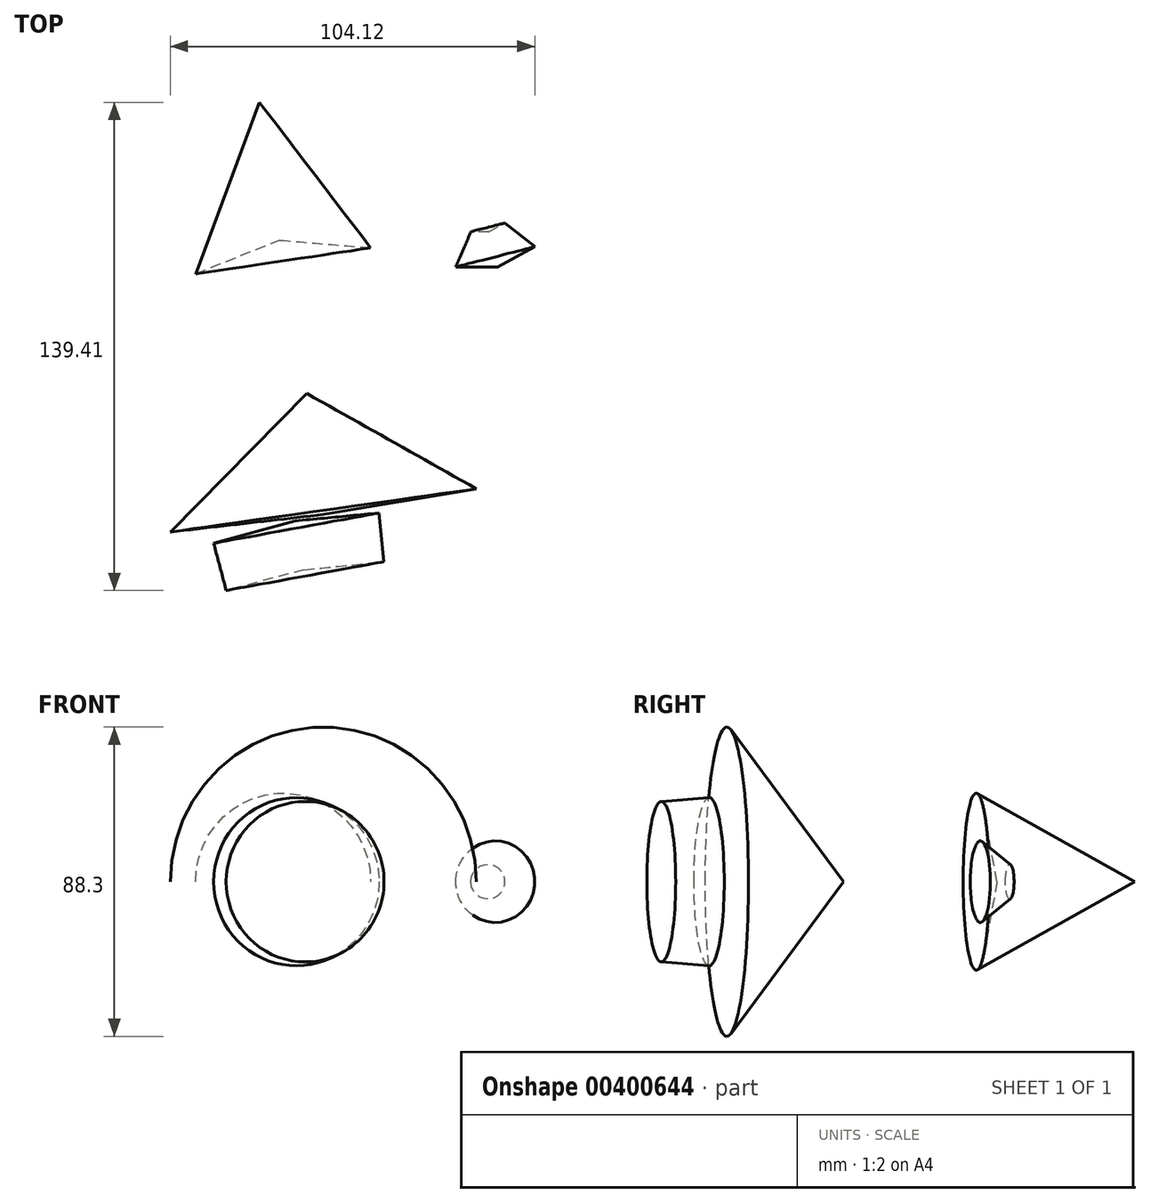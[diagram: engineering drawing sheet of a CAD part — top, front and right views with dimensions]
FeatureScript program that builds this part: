
annotation { "Feature Type Name" : "Feature", "Feature Type Description" : "" }
export const myFeature = defineFeature(function(context is Context, id is Id, definition is map)
    precondition{}
    {
        {
            var Q0;
            Q0=qCreatedBy(makeId("Top.planeOp"),FACE);
            var sketch = newSketch(context, id + "F0", { "sketchPlane" : qUnion([Q0])});
            skLineSegment(sketch, "E0", {"start": v(-35.58, 73.22) * mm, "end": v(-13.14, -77.38) * mm});
            skLineSegment(sketch, "E1", {"start": v(-35.58, 73.22) * mm, "end": v(-3.81, 31.64) * mm});
            skLineSegment(sketch, "E2", {"start": v(-3.81, 31.64) * mm, "end": v(-29.71, 33.85) * mm});
            skLineSegment(sketch, "E3", {"start": v(-29.71, 33.85) * mm, "end": v(15.1, -14.55) * mm});
            skLineSegment(sketch, "E4", {"start": v(15.1, -14.55) * mm, "end": v(-22.5, -14.55) * mm});
            skLineSegment(sketch, "E5", {"start": v(-22.5, -14.55) * mm, "end": v(29.76, -76.58) * mm});
            skLineSegment(sketch, "E6", {"start": v(29.76, -76.58) * mm, "end": v(-13.14, -77.38) * mm});
            skSolve(sketch);
        }
        {
            var Q0;
            {var subQ0=sQuery(id+"F0.wireOp",EDGE,"E1");Q0=makeQuery(id+"F0.imprint","IMPRINT",FACE,{"disambiguationData":[TD([[makeQuery(id+"F0.imprint","IMPRINT",EDGE,{"derivedFrom":subQ0}),-1.0]])]});}
            var Q1;
            Q1=sQuery(id+"F0.wireOp",EDGE,"E0");
            revolve(context, id + "F1", {"entities" : qUnion([Q0]), "axis" : qUnion([Q1]), "revolveType" : RevolveType.FULL});
        }
        {
            var Q0;
            Q0=qCreatedBy(makeId("Top.planeOp"),FACE);
            var sketch = newSketch(context, id + "F2", { "sketchPlane" : qUnion([Q0])});
            skLineSegment(sketch, "E7", {"start": v(-26.84, 26.16) * mm, "end": v(-22.02, -14.83) * mm});
            skLineSegment(sketch, "E8", {"start": v(-22.02, -14.83) * mm, "end": v(-26.84, 26.16) * mm});
            skLineSegment(sketch, "E9", {"start": v(-26.84, 26.16) * mm, "end": v(6.69, -4.52) * mm});
            skLineSegment(sketch, "E10", {"start": v(6.69, -4.52) * mm, "end": v(-22.02, -14.83) * mm});
            skSolve(sketch);
        }
        {
            var Q0;
            Q0=sQuery(id+"F2.wireOp",EDGE,"E9");
            var Q1;
            Q1=sQuery(id+"F2.wireOp",EDGE,"E8");
            revolve(context, id + "F3", {"bodyType" : ToolBodyType.SURFACE, "surfaceEntities" : qUnion([Q0]), "axis" : qUnion([Q1]), "revolveType" : RevolveType.FULL});
        }
        {
            var Q0;
            Q0=qCreatedBy(makeId("Top.planeOp"),FACE);
            var sketch = newSketch(context, id + "F4", { "sketchPlane" : qUnion([Q0])});
            skLineSegment(sketch, "E11", {"start": v(-22.05, -9.93) * mm, "end": v(-17.17, -44.48) * mm});
            skLineSegment(sketch, "E12", {"start": v(-22.05, -9.93) * mm, "end": v(26.38, -37.14) * mm});
            skLineSegment(sketch, "E13", {"start": v(26.38, -37.14) * mm, "end": v(-17.17, -44.48) * mm});
            skSolve(sketch);
        }
        {
            var Q0;
            Q0=makeQuery(id+"F4.imprint","IMPRINT",FACE,{"disambiguationData":[TD([[makeQuery(id+"F4.imprint","IMPRINT",EDGE,{"derivedFrom":sQuery(id+"F4.wireOp",EDGE,"E11")}),1.0]])]});
            var Q1;
            Q1=sQuery(id+"F4.wireOp",EDGE,"E11");
            revolve(context, id + "F5", {"entities" : qUnion([Q0]), "axis" : qUnion([Q1]), "revolveType" : RevolveType.FULL});
        }
        {
            var Q0;
            Q0=qCreatedBy(makeId("Top.planeOp"),FACE);
            var sketch = newSketch(context, id + "F6", { "sketchPlane" : qUnion([Q0])});
            skLineSegment(sketch, "E14", {"start": v(-25.42, -46.31) * mm, "end": v(-22.86, -60.3) * mm});
            skLineSegment(sketch, "E15", {"start": v(-22.86, -60.3) * mm, "end": v(0, -57.94) * mm});
            skLineSegment(sketch, "E16", {"start": v(0, -57.94) * mm, "end": v(-1.43, -44.07) * mm});
            skLineSegment(sketch, "E17", {"start": v(-1.43, -44.07) * mm, "end": v(-25.42, -46.31) * mm});
            skSolve(sketch);
        }
        {
            var Q0;
            Q0=makeQuery(id+"F6.imprint","IMPRINT",FACE,{"disambiguationData":[TD([[makeQuery(id+"F6.imprint","IMPRINT",EDGE,{"derivedFrom":sQuery(id+"F6.wireOp",EDGE,"E14")}),1.0]])]});
            var Q1;
            Q1=sQuery(id+"F6.wireOp",EDGE,"E14");
            revolve(context, id + "F7", {"entities" : qUnion([Q0]), "axis" : qUnion([Q1]), "revolveType" : RevolveType.FULL});
        }
        {
            var Q0;
            Q0=qCreatedBy(makeId("Top.planeOp"),FACE);
            var sketch = newSketch(context, id + "F8", { "sketchPlane" : qUnion([Q0])});
            skLineSegment(sketch, "E18", {"start": v(24.83, 36.26) * mm, "end": v(20.5, 26.21) * mm});
            skLineSegment(sketch, "E19", {"start": v(20.5, 26.21) * mm, "end": v(32.52, 26.21) * mm});
            skLineSegment(sketch, "E20", {"start": v(24.83, 36.26) * mm, "end": v(29.95, 36.26) * mm});
            skLineSegment(sketch, "E21", {"start": v(29.95, 36.26) * mm, "end": v(32.52, 26.21) * mm});
            skLineSegment(sketch, "E22", {"start": v(24.83, 36.26) * mm, "end": v(27.4, 40.6) * mm});
            skPoint(sketch, "E22.endSnap0", {"position": v(27.4, 36.26) * mm});
            skLineSegment(sketch, "E23", {"start": v(29.95, 36.26) * mm, "end": v(27.4, 40.6) * mm});
            skPoint(sketch, "E24.6.internal.snap0", {"position": v(28.67, 38.43) * mm});
            skFitSpline(sketch, "E24", {"points": [v(27.4, 40.6) * mm, v(24.44, 40.6) * mm, v(23.06, 42.37) * mm, v(23.65, 44.54) * mm, v(25.03, 45.52) * mm, v(27.4, 45.72) * mm, v(28.67, 43.95) * mm, v(27.4, 40.6) * mm]});
            skSolve(sketch);
        }
        {
            var Q0;
            Q0=makeQuery(id+"F8.imprint","IMPRINT",FACE,{"disambiguationData":[TD([[makeQuery(id+"F8.imprint","IMPRINT",EDGE,{"derivedFrom":sQuery(id+"F8.wireOp",EDGE,"E18")}),1.0]])]});
            var Q1;
            Q1=sQuery(id+"F8.wireOp",EDGE,"E21");
            revolve(context, id + "F9", {"entities" : qUnion([Q0]), "axis" : qUnion([Q1]), "revolveType" : RevolveType.FULL});
        }
    });
